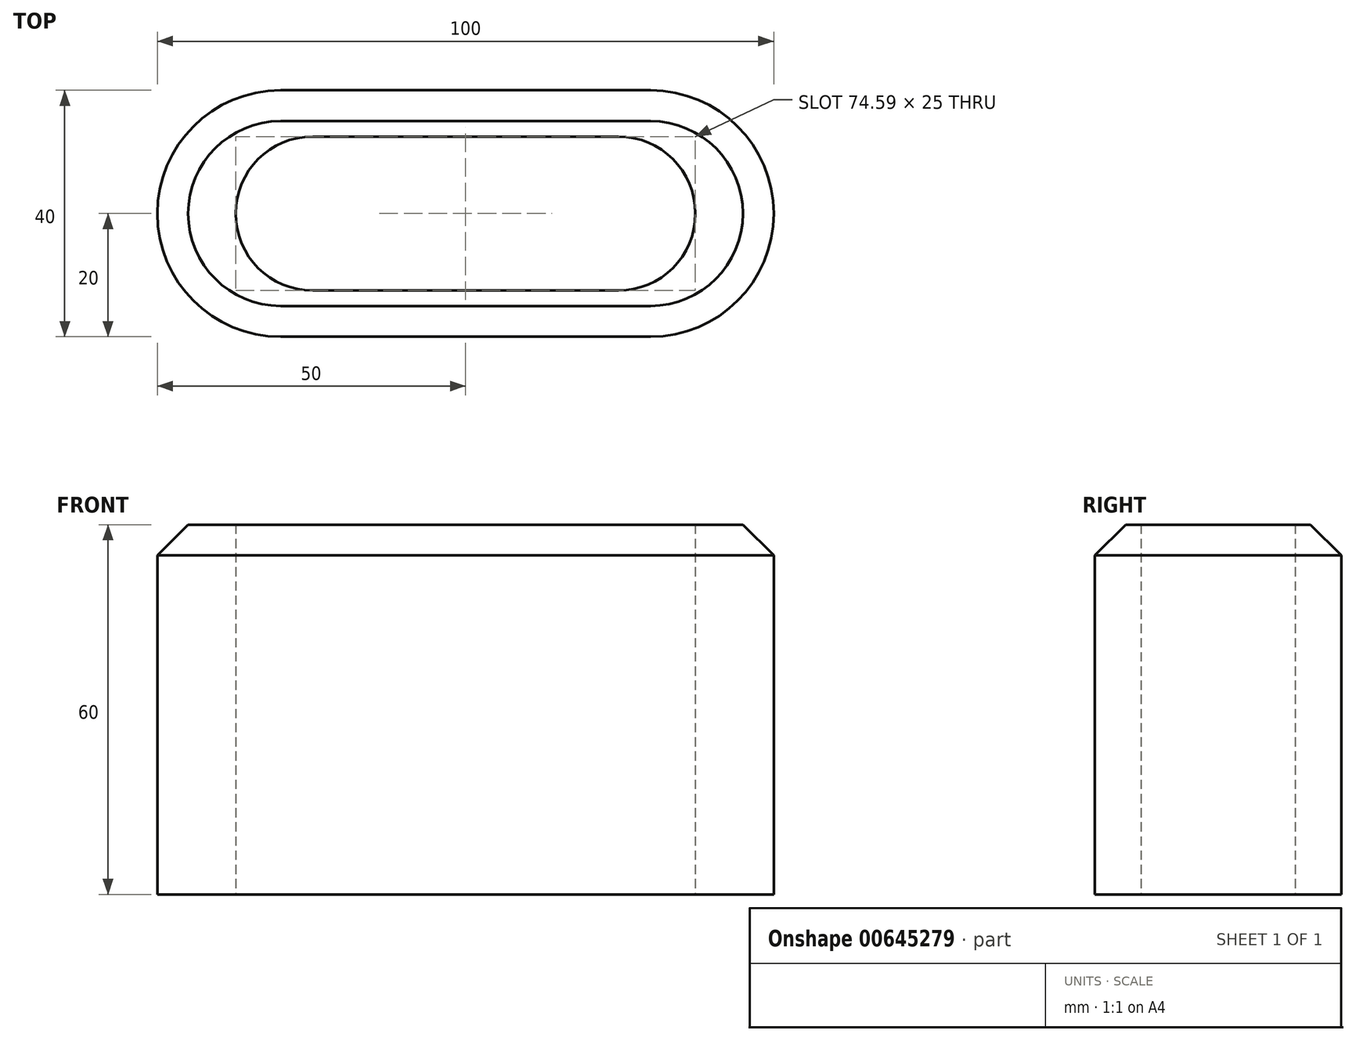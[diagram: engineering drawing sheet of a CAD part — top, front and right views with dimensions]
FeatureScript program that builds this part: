
annotation { "Feature Type Name" : "Feature", "Feature Type Description" : "" }
export const myFeature = defineFeature(function(context is Context, id is Id, definition is map)
    precondition{}
    {
        {
            var Q0;
            Q0=qCreatedBy(makeId("Top.planeOp"),FACE);
            var sketch = newSketch(context, id + "F0", { "sketchPlane" : qUnion([Q0])});
            skLineSegment(sketch, "E0.0", {"start": v(0, 20) * mm, "end": v(30, 20) * mm});
            skLineSegment(sketch, "E1", {"start": v(0, 0) * mm, "end": v(0, 71.3) * mm, "construction": true});
            skLineSegment(sketch, "E2.0", {"start": v(0, -20) * mm, "end": v(30, -20) * mm});
            skArc(sketch, "E3", {"start": v(30, -20) * mm, "mid": v(50, 0) * mm, "end": v(30, 20) * mm});
            skLineSegment(sketch, "E4.MirrorCS", {"start": v(0, 20) * mm, "end": v(-30, 20) * mm});
            skArc(sketch, "E5.MirrorCS", {"start": v(-30, -20) * mm, "mid": v(-50, 0) * mm, "end": v(-30, 20) * mm});
            skLineSegment(sketch, "E6.MirrorCS", {"start": v(0, -20) * mm, "end": v(-30, -20) * mm});
            skLineSegment(sketch, "E7.0", {"start": v(0, 15) * mm, "end": v(30, 15) * mm});
            skArc(sketch, "E7.1", {"start": v(-30, -15) * mm, "mid": v(-45, 0) * mm, "end": v(-30, 15) * mm});
            skLineSegment(sketch, "E7.2", {"start": v(0, -15) * mm, "end": v(-30, -15) * mm});
            skLineSegment(sketch, "E7.3", {"start": v(0, 15) * mm, "end": v(-30, 15) * mm});
            skLineSegment(sketch, "E7.4", {"start": v(0, -15) * mm, "end": v(30, -15) * mm});
            skArc(sketch, "E7.5", {"start": v(30, -15) * mm, "mid": v(45, 0) * mm, "end": v(30, 15) * mm});
            skLineSegment(sketch, "E8", {"start": v(0, 0) * mm, "end": v(0, -8.16) * mm});
            skLineSegment(sketch, "E9.0", {"start": v(0, -12.5) * mm, "end": v(24.8, -12.5) * mm});
            skLineSegment(sketch, "E10.0", {"start": v(0, 12.5) * mm, "end": v(24.8, 12.5) * mm});
            skArc(sketch, "E11", {"start": v(24.8, -12.5) * mm, "mid": v(37.3, 0) * mm, "end": v(24.8, 12.5) * mm});
            skLineSegment(sketch, "E12.MirrorCS", {"start": v(0, 12.5) * mm, "end": v(-24.8, 12.5) * mm});
            skArc(sketch, "E13.MirrorCS", {"start": v(-24.8, -12.5) * mm, "mid": v(-37.3, 0) * mm, "end": v(-24.8, 12.5) * mm});
            skLineSegment(sketch, "E14.MirrorCS", {"start": v(0, -12.5) * mm, "end": v(-24.8, -12.5) * mm});
            skSolve(sketch);
        }
        {
            var Q0;
            Q0=makeQuery(id+"F0.imprint","IMPRINT",FACE,{"disambiguationData":[TD([[makeQuery(id+"F0.imprint","IMPRINT",EDGE,{"derivedFrom":sQuery(id+"F0.wireOp",EDGE,"E7.0")}),-1.0]])]});
            var Q1;
            Q1=makeQuery(id+"F0.imprint","IMPRINT",FACE,{"disambiguationData":[TD([[makeQuery(id+"F0.imprint","IMPRINT",EDGE,{"derivedFrom":sQuery(id+"F0.wireOp",EDGE,"E0.0")}),-1.0]])]});
            extrude(context, id + "F1", {"entities" : qUnion([Q0, Q1]), "depth" : 60 * mm, "offsetDistance" : 25 * mm});
        }
        {
            var Q0;
            Q0=makeQuery(id+"F1.opExtrude","CAP_EDGE",EDGE,{"disambiguationData":[OSD([sQuery(id+"F0.wireOp",EDGE,"E5.MirrorCS")])],"isStart":false});
            chamfer(context, id + "F2", {"entities" : qUnion([Q0]), "chamferType" : ChamferType.OFFSET_ANGLE, "width" : 5 * mm, "oppositeDirection" : false, "angle" : 45 * degree, "tangentPropagation" : true});
        }
    });
